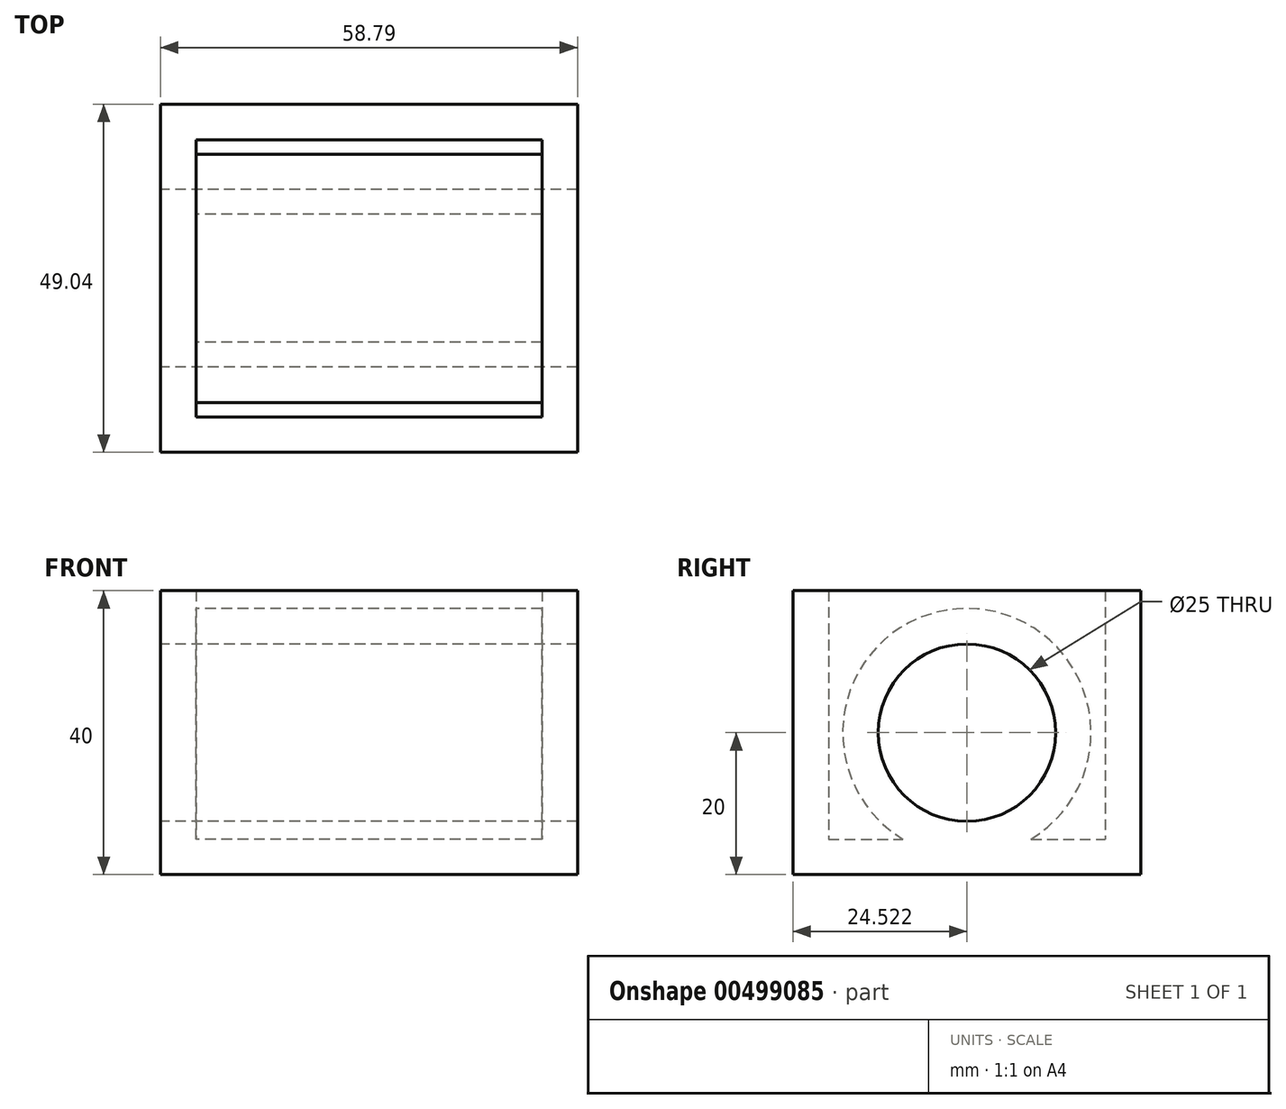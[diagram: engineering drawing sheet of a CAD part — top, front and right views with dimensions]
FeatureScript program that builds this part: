
annotation { "Feature Type Name" : "Feature", "Feature Type Description" : "" }
export const myFeature = defineFeature(function(context is Context, id is Id, definition is map)
    precondition{}
    {
        {
            var Q0;
            Q0=qCreatedBy(makeId("Top.planeOp"),FACE);
            var sketch = newSketch(context, id + "F0", { "sketchPlane" : qUnion([Q0])});
            skLineSegment(sketch, "E0.bottom", {"start": v(0, 0) * mm, "end": v(58.8, 0) * mm});
            skLineSegment(sketch, "E0.top", {"start": v(0, 49.04) * mm, "end": v(58.8, 49.04) * mm});
            skLineSegment(sketch, "E0.left", {"start": v(0, 0) * mm, "end": v(0, 49.04) * mm});
            skLineSegment(sketch, "E0.right", {"start": v(58.8, 0) * mm, "end": v(58.8, 49.04) * mm});
            skSolve(sketch);
        }
        {
            var Q0;
            Q0 = qSketchRegion(id + "F0", true);
            extrude(context, id + "F1", {"entities" : qUnion([Q0]), "depth" : 40 * mm});
        }
        {
            var Q0;
            Q0=makeQuery(id+"F1.opExtrude","SWEPT_FACE",FACE,{"disambiguationData":[OSD([sQuery(id+"F0.wireOp",EDGE,"E0.left")])]});
            var sketch = newSketch(context, id + "F2", { "sketchPlane" : qUnion([Q0])});
            skCircle(sketch, "E1", {"center": v(-24.52, 20) * mm, "radius": 12.5 * mm});
            skPoint(sketch, "E1.centerSnap0", {"position": v(0, 20) * mm});
            skPoint(sketch, "E1.centerSnap1", {"position": v(-24.52, 0) * mm});
            skSolve(sketch);
        }
        {
            var Q0;
            Q0 = qSketchRegion(id + "F2", true);
            extrude(context, id + "F3", {"entities" : qUnion([Q0]), "operationType" : NewBodyOperationType.REMOVE, "endBound" : BoundingType.UP_TO_NEXT, "oppositeDirection" : true, "depth" : 25 * mm});
        }
        {
            var Q0;
            Q0=makeQuery(id+"F1.opExtrude","CAP_FACE",FACE,{"disambiguationData":[OSD([sQuery(id+"F0.wireOp",EDGE,"E0.bottom"),sQuery(id+"F0.wireOp",EDGE,"E0.top"),sQuery(id+"F0.wireOp",EDGE,"E0.left"),sQuery(id+"F0.wireOp",EDGE,"E0.right")])],"isStart":false});
            shell(context, id + "F4", {"entities" : qUnion([Q0]), "thickness" : 5 * mm});
        }
    });
